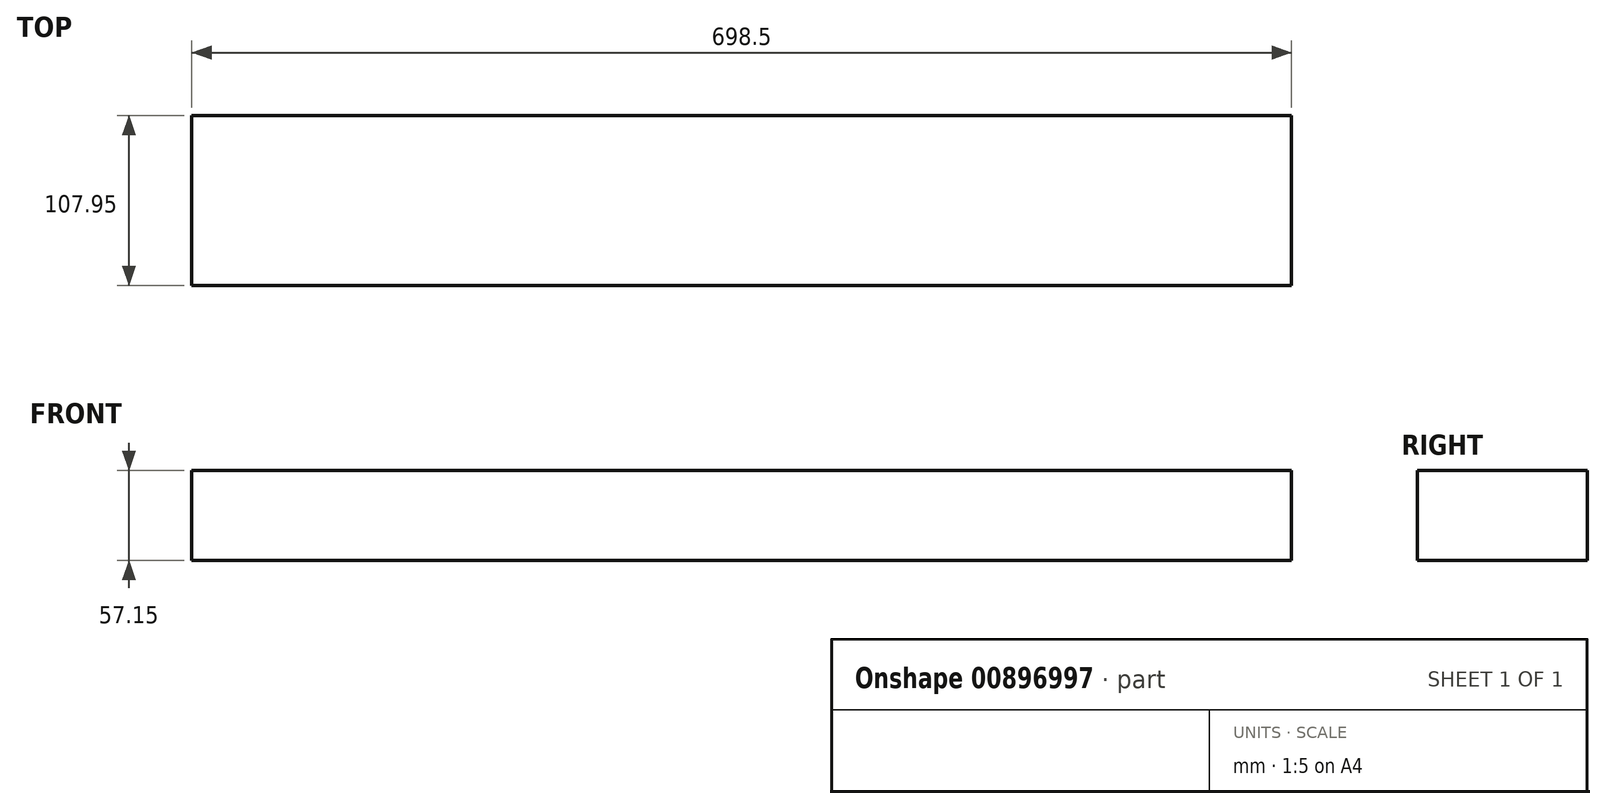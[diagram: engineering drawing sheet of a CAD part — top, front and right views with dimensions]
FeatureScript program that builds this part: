
annotation { "Feature Type Name" : "Feature", "Feature Type Description" : "" }
export const myFeature = defineFeature(function(context is Context, id is Id, definition is map)
    precondition{}
    {
        {
            var Q0;
            Q0=qCreatedBy(makeId("Top.planeOp"),FACE);
            var sketch = newSketch(context, id + "F0", { "sketchPlane" : qUnion([Q0])});
            skLineSegment(sketch, "E0.bottom", {"start": v(0, 0) * mm, "end": v(698.5, 0) * mm});
            skLineSegment(sketch, "E0.top", {"start": v(0, 107.95) * mm, "end": v(698.5, 107.95) * mm});
            skLineSegment(sketch, "E0.left", {"start": v(0, 0) * mm, "end": v(0, 107.95) * mm});
            skLineSegment(sketch, "E0.right", {"start": v(698.5, 0) * mm, "end": v(698.5, 107.95) * mm});
            skSolve(sketch);
        }
        {
            var Q0;
            Q0 = qSketchRegion(id + "F0", true);
            extrude(context, id + "F1", {"entities" : qUnion([Q0]), "depth" : 57.15 * mm, "offsetDistance" : 25.4 * mm});
        }
    });
